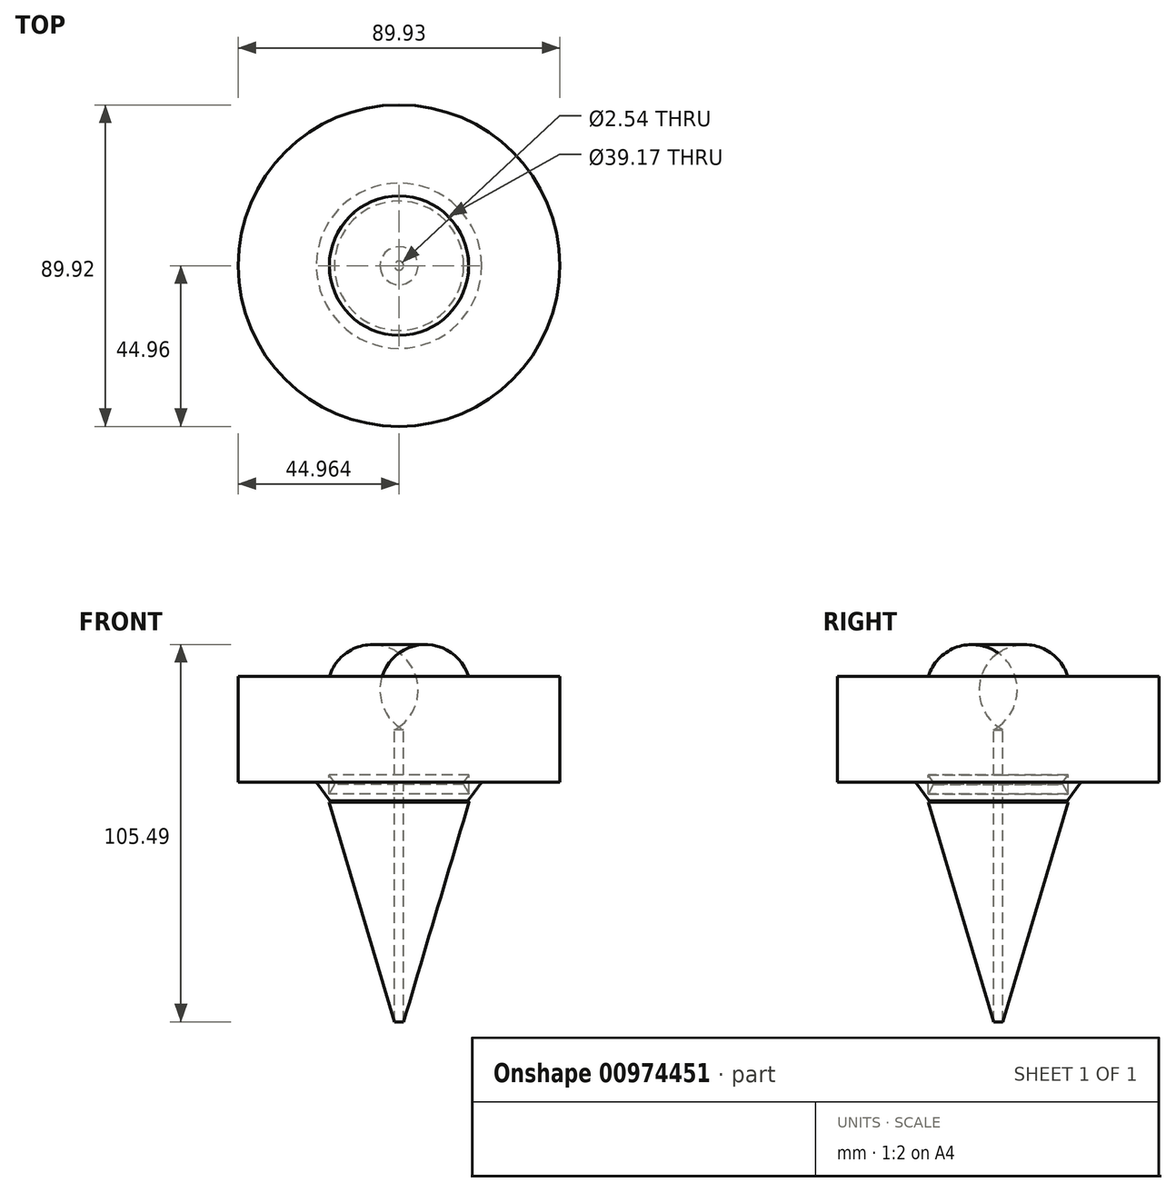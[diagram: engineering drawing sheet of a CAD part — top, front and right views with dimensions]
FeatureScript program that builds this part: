
annotation { "Feature Type Name" : "Feature", "Feature Type Description" : "" }
export const myFeature = defineFeature(function(context is Context, id is Id, definition is map)
    precondition{}
    {
        {
            var Q0;
            Q0=qCreatedBy(makeId("Front.planeOp"),FACE);
            var sketch = newSketch(context, id + "F0", { "sketchPlane" : qUnion([Q0])});
            skLineSegment(sketch, "E0", {"start": v(-47.7, 30.3) * mm, "end": v(-47.7, 0.67) * mm});
            skLineSegment(sketch, "E1", {"start": v(-47.7, 0.67) * mm, "end": v(-4, 0.67) * mm});
            skLineSegment(sketch, "E2", {"start": v(-4, 0.67) * mm, "end": v(-4, 15.31) * mm});
            skLineSegment(sketch, "E3", {"start": v(-47.7, 30.3) * mm, "end": v(-22.2, 30.3) * mm});
            skArc(sketch, "E4", {"start": v(-22.2, 30.3) * mm, "mid": v(-18.18, 16.65) * mm, "end": v(-4, 15.31) * mm});
            skLineSegment(sketch, "E5", {"start": v(-2.74, 39.96) * mm, "end": v(-2.74, 8.44) * mm});
            skLineSegment(sketch, "E6", {"start": v(-2.74, 8.44) * mm, "end": v(-2.74, 0) * mm});
            skLineSegment(sketch, "E7", {"start": v(-21.18, 0.67) * mm, "end": v(-20.8, 0) * mm});
            skLineSegment(sketch, "E8", {"start": v(-20.8, 0) * mm, "end": v(-20.8, 0.67) * mm});
            skLineSegment(sketch, "E9", {"start": v(-20.8, 0.67) * mm, "end": v(-22.32, 2.72) * mm});
            skLineSegment(sketch, "E10", {"start": v(-22.32, 2.72) * mm, "end": v(-22.32, -2.63) * mm});
            skLineSegment(sketch, "E11", {"start": v(-22.32, -2.63) * mm, "end": v(-20.8, 0) * mm});
            skLineSegment(sketch, "E12", {"start": v(-22.32, -4.95) * mm, "end": v(-25.85, 0.67) * mm});
            skLineSegment(sketch, "E13", {"start": v(-25.85, 0.67) * mm, "end": v(-22.02, -4.5) * mm});
            skLineSegment(sketch, "E14", {"start": v(-22.02, -4.5) * mm, "end": v(-22.32, -2.63) * mm});
            skLineSegment(sketch, "E15", {"start": v(-22.02, -4.5) * mm, "end": v(-22.32, -4.95) * mm});
            skLineSegment(sketch, "E16", {"start": v(-4, 0.67) * mm, "end": v(-4, -66.34) * mm});
            skLineSegment(sketch, "E17", {"start": v(-4, -66.34) * mm, "end": v(-22.32, -4.95) * mm});
            skSolve(sketch);
        }
        {
            var Q0;
            {var subQ0=sQuery(id+"F0.wireOp",EDGE,"E8");Q0=makeQuery(id+"F0.imprint","IMPRINT",FACE,{"disambiguationData":[TD([[makeQuery(id+"F0.imprint","IMPRINT",EDGE,{"derivedFrom":subQ0}),-1.0]])]});}
            var Q1;
            {var subQ0=sQuery(id+"F0.wireOp",EDGE,"E13");Q1=makeQuery(id+"F0.imprint","IMPRINT",FACE,{"disambiguationData":[TD([[makeQuery(id+"F0.imprint","IMPRINT",EDGE,{"derivedFrom":subQ0}),1.0]])]});}
            var Q2;
            {var subQ4=sQuery(id+"F0.wireOp",EDGE,"E0");Q2=makeQuery(id+"F0.imprint","IMPRINT",FACE,{"disambiguationData":[TD([[makeQuery(id+"F0.imprint","IMPRINT",EDGE,{"derivedFrom":subQ4}),1.0]])]});}
            var Q3;
            Q3=sQuery(id+"F0.wireOp",EDGE,"E17");
            var Q4;
            Q4=sQuery(id+"F0.wireOp",EDGE,"E16");
            var Q5;
            Q5=sQuery(id+"F0.wireOp",EDGE,"E2");
            var Q6;
            Q6=sQuery(id+"F0.wireOp",EDGE,"E4");
            var Q7;
            Q7=sQuery(id+"F0.wireOp",EDGE,"E0");
            var Q8;
            Q8=sQuery(id+"F0.wireOp",EDGE,"E1");
            var Q9;
            Q9=sQuery(id+"F0.wireOp",EDGE,"E12");
            var Q10;
            Q10=sQuery(id+"F0.wireOp",EDGE,"E3");
            var Q11;
            Q11=sQuery(id+"F0.wireOp",EDGE,"E6");
            revolve(context, id + "F1", {"surfaceOperationType" : NewSurfaceOperationType.NEW, "entities" : qUnion([Q0, Q1, Q2]), "surfaceEntities" : qUnion([Q3, Q4, Q5, Q6, Q7, Q8, Q9, Q10]), "axis" : qUnion([Q11]), "revolveType" : RevolveType.FULL});
        }
    });
